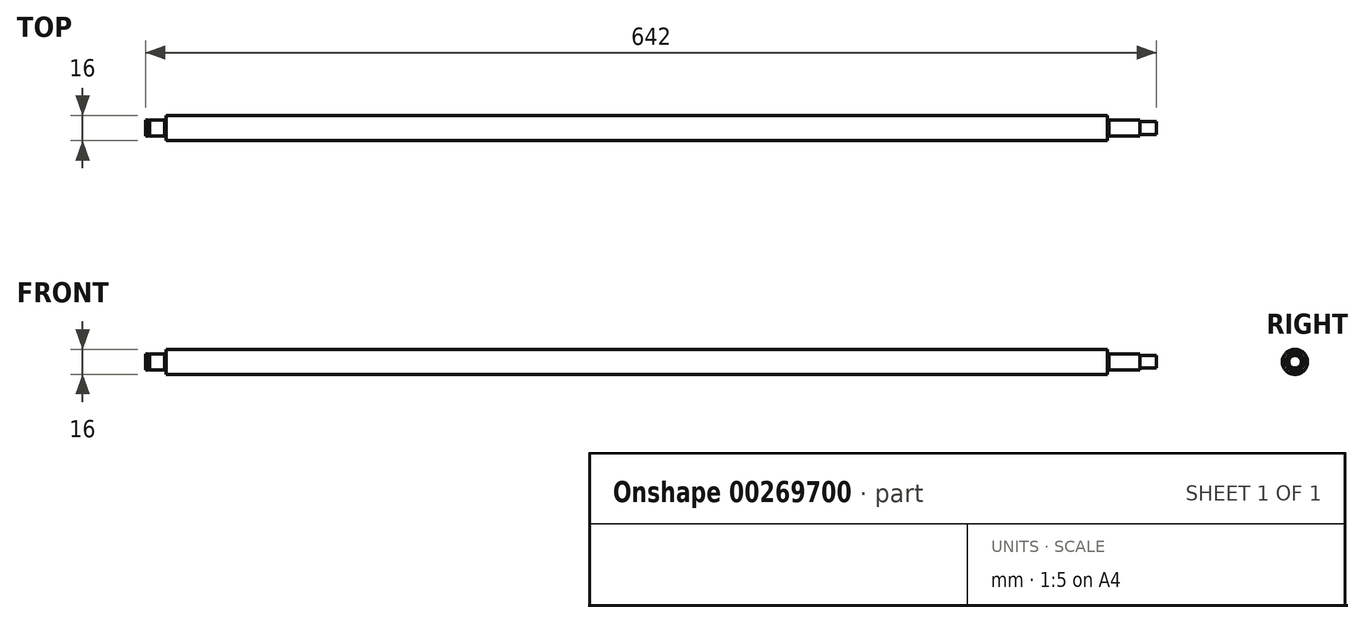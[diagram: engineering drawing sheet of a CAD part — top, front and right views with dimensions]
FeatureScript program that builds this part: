
annotation { "Feature Type Name" : "Feature", "Feature Type Description" : "" }
export const myFeature = defineFeature(function(context is Context, id is Id, definition is map)
    precondition{}
    {
        {
            var Q0;
            Q0=qCreatedBy(makeId("Front.planeOp"),FACE);
            var sketch = newSketch(context, id + "F0", { "sketchPlane" : qUnion([Q0])});
            skLineSegment(sketch, "E0", {"start": v(-313, 0) * mm, "end": v(329, 0) * mm});
            skLineSegment(sketch, "E1", {"start": v(329, 0) * mm, "end": v(329, 4) * mm});
            skLineSegment(sketch, "E2", {"start": v(329, 4) * mm, "end": v(318.5, 4) * mm});
            skLineSegment(sketch, "E3", {"start": v(318.5, 4) * mm, "end": v(318.5, 5) * mm});
            skLineSegment(sketch, "E4", {"start": v(318.5, 5) * mm, "end": v(299, 5) * mm});
            skLineSegment(sketch, "E5", {"start": v(299, 5) * mm, "end": v(299, 6) * mm});
            skLineSegment(sketch, "E6", {"start": v(299, 6) * mm, "end": v(298, 6) * mm});
            skLineSegment(sketch, "E7", {"start": v(298, 6) * mm, "end": v(298, 8) * mm});
            skLineSegment(sketch, "E8", {"start": v(298, 8) * mm, "end": v(-300, 8) * mm});
            skLineSegment(sketch, "E9", {"start": v(-300, 8) * mm, "end": v(-300, 6) * mm});
            skLineSegment(sketch, "E10", {"start": v(-300, 6) * mm, "end": v(-301, 6) * mm});
            skLineSegment(sketch, "E11", {"start": v(-301, 6) * mm, "end": v(-301, 5) * mm});
            skLineSegment(sketch, "E12", {"start": v(-301, 5) * mm, "end": v(-310.6, 5) * mm});
            skLineSegment(sketch, "E13", {"start": v(-310.6, 5) * mm, "end": v(-310.6, 4.8) * mm});
            skLineSegment(sketch, "E14", {"start": v(-310.6, 4.8) * mm, "end": v(-311.1, 4.8) * mm});
            skLineSegment(sketch, "E15", {"start": v(-311.1, 4.8) * mm, "end": v(-311.1, 5) * mm});
            skLineSegment(sketch, "E16", {"start": v(-311.1, 5) * mm, "end": v(-313, 5) * mm});
            skLineSegment(sketch, "E17", {"start": v(-313, 5) * mm, "end": v(-313, 0) * mm});
            skSolve(sketch);
        }
        {
            var Q0;
            Q0=makeQuery(id+"F0.imprint","IMPRINT",FACE,{"disambiguationData":[TD([[makeQuery(id+"F0.imprint","IMPRINT",EDGE,{"derivedFrom":sQuery(id+"F0.wireOp",EDGE,"E0")}),1.0]])]});
            var Q1;
            Q1=sQuery(id+"F0.wireOp",EDGE,"E0");
            revolve(context, id + "F1", {"entities" : qUnion([Q0]), "axis" : qUnion([Q1]), "revolveType" : RevolveType.FULL});
        }
    });
